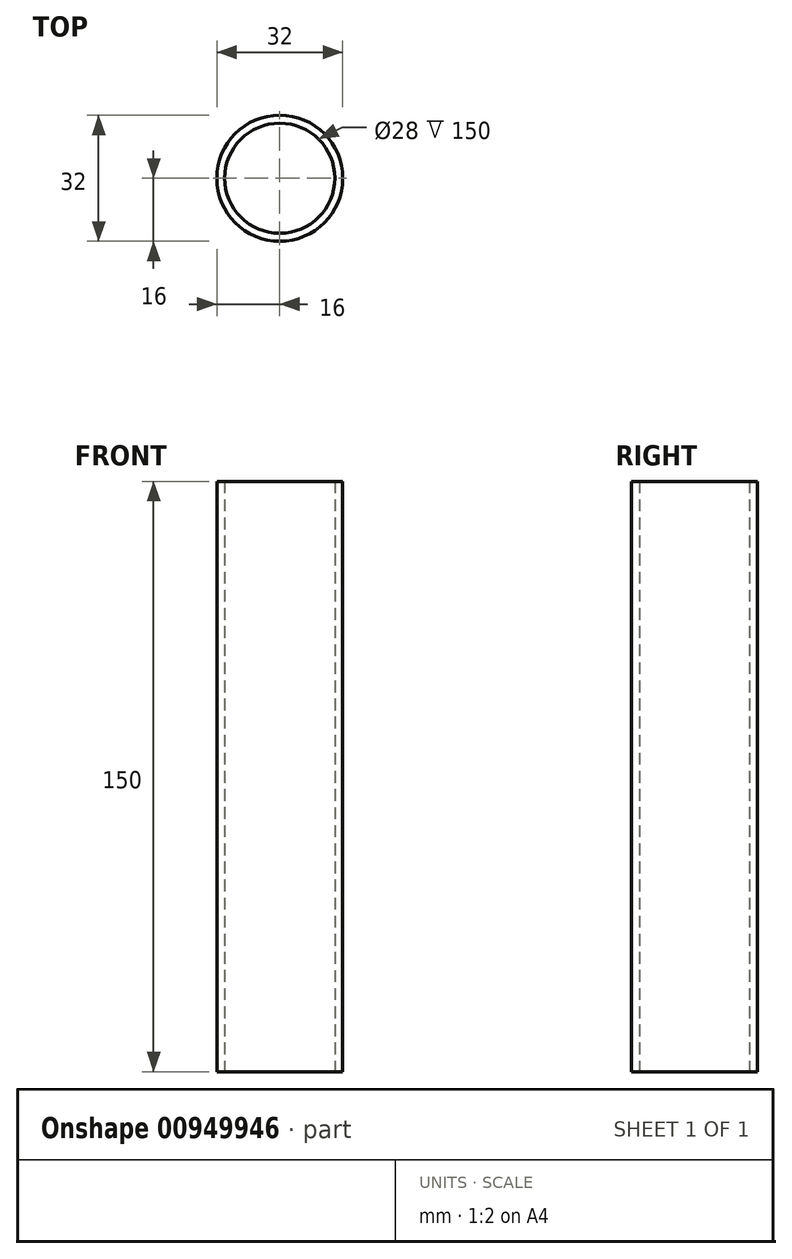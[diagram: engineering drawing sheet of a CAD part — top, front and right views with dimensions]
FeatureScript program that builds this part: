
annotation { "Feature Type Name" : "Feature", "Feature Type Description" : "" }
export const myFeature = defineFeature(function(context is Context, id is Id, definition is map)
    precondition{}
    {
        {
            var Q0;
            Q0=qCreatedBy(makeId("Top.planeOp"),FACE);
            var sketch = newSketch(context, id + "F0", { "sketchPlane" : qUnion([Q0])});
            skCircle(sketch, "E0", {"center": v(0, 0) * mm, "radius": 14 * mm});
            skCircle(sketch, "E1", {"center": v(0, 0) * mm, "radius": 16 * mm});
            skSolve(sketch);
        }
        {
            var Q0;
            Q0=makeQuery(id+"F0.imprint","IMPRINT",FACE,{"disambiguationData":[TD([[makeQuery(id+"F0.imprint","IMPRINT",EDGE,{"derivedFrom":sQuery(id+"F0.wireOp",EDGE,"E0")}),-1.0]])]});
            extrude(context, id + "F1", {"entities" : qUnion([Q0]), "flatOperationType" : FlatOperationType.REMOVE, "depth" : 150 * mm, "offsetDistance" : 25 * mm, "domain" : OperationDomain.MODEL});
        }
    });
